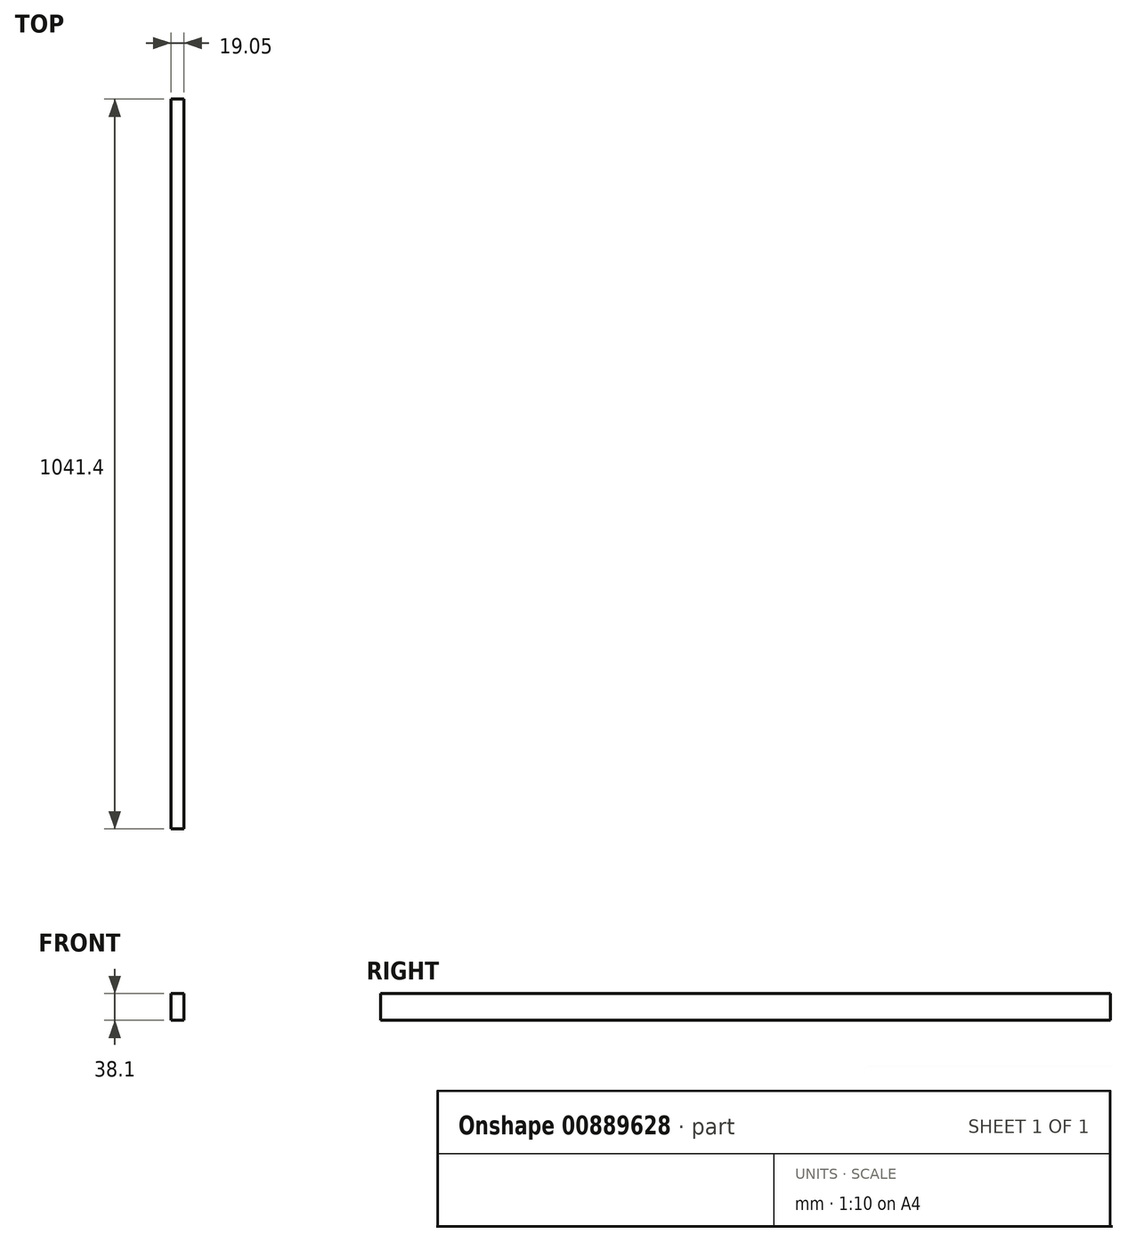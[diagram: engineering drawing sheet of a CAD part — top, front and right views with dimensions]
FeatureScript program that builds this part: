
annotation { "Feature Type Name" : "Feature", "Feature Type Description" : "" }
export const myFeature = defineFeature(function(context is Context, id is Id, definition is map)
    precondition{}
    {
        {
            var Q0;
            Q0=qCreatedBy(makeId("Front.planeOp"),FACE);
            var sketch = newSketch(context, id + "F0", { "sketchPlane" : qUnion([Q0])});
            skLineSegment(sketch, "E0.bottom", {"start": v(0, 0) * mm, "end": v(19.05, 0) * mm});
            skLineSegment(sketch, "E0.top", {"start": v(0, 38.1) * mm, "end": v(19.05, 38.1) * mm});
            skLineSegment(sketch, "E0.left", {"start": v(0, 0) * mm, "end": v(0, 38.1) * mm});
            skLineSegment(sketch, "E0.right", {"start": v(19.05, 0) * mm, "end": v(19.05, 38.1) * mm});
            skSolve(sketch);
        }
        {
            var Q0;
            Q0 = qSketchRegion(id + "F0", true);
            extrude(context, id + "F1", {"entities" : qUnion([Q0]), "depth" : 1041.4 * mm, "offsetDistance" : 25.4 * mm});
        }
    });
